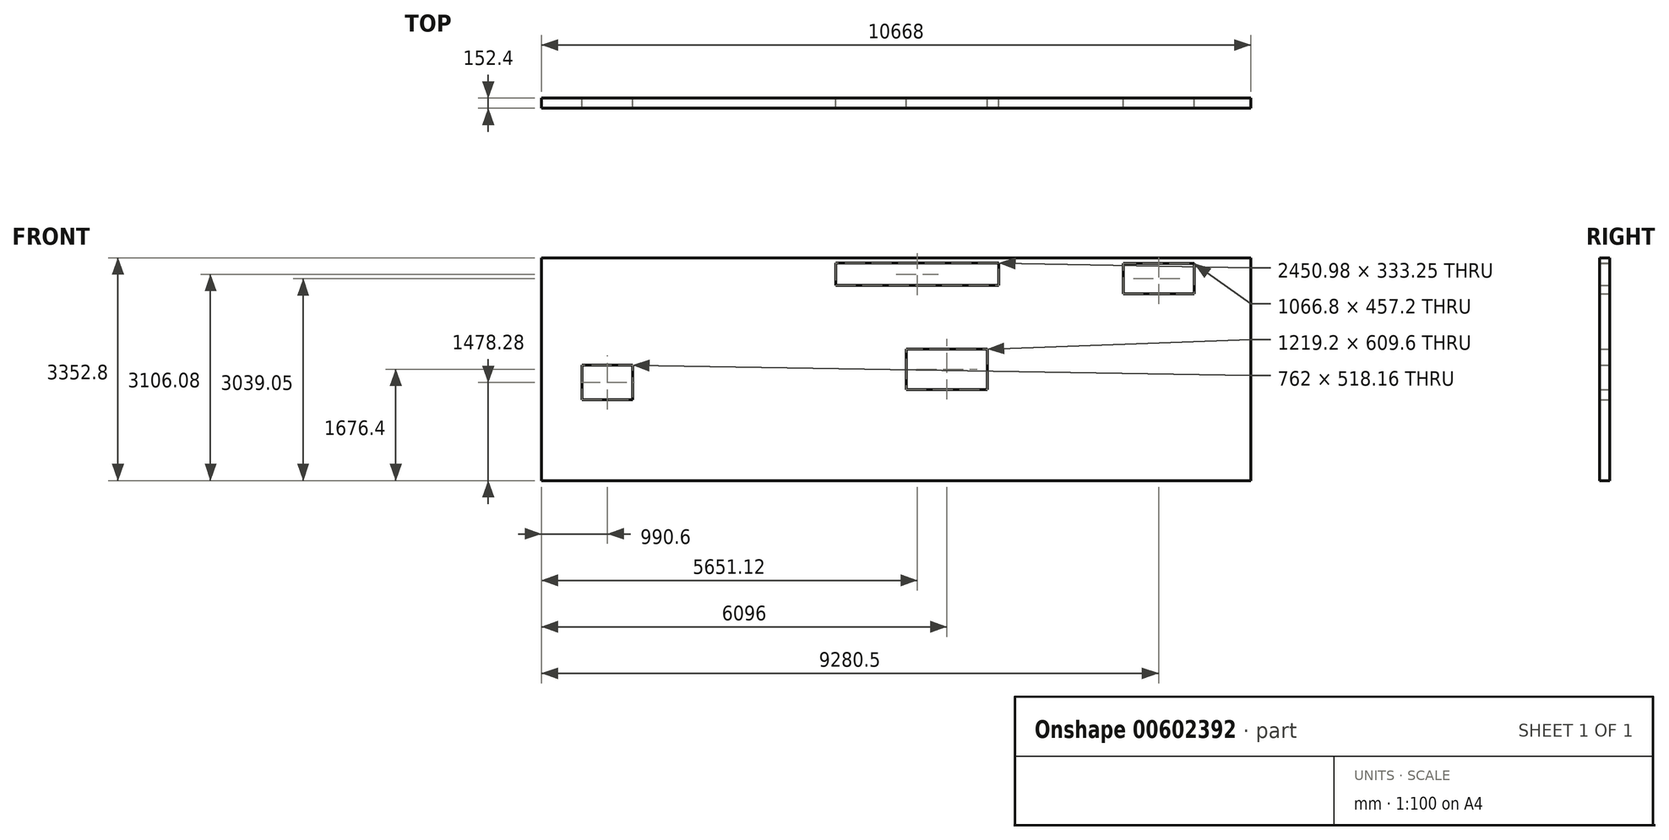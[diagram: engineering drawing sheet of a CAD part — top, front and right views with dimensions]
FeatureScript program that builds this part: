
annotation { "Feature Type Name" : "Feature", "Feature Type Description" : "" }
export const myFeature = defineFeature(function(context is Context, id is Id, definition is map)
    precondition{}
    {
        {
            var Q0;
            Q0=qCreatedBy(makeId("Front.planeOp"),FACE);
            var sketch = newSketch(context, id + "F0", { "sketchPlane" : qUnion([Q0])});
            skLineSegment(sketch, "E0.bottom", {"start": v(-5334, 1676.4) * mm, "end": v(5334, 1676.4) * mm});
            skLineSegment(sketch, "E0.top", {"start": v(-5334, -1676.4) * mm, "end": v(5334, -1676.4) * mm});
            skLineSegment(sketch, "E0.left", {"start": v(-5334, 1676.4) * mm, "end": v(-5334, -1676.4) * mm});
            skLineSegment(sketch, "E0.right", {"start": v(5334, 1676.4) * mm, "end": v(5334, -1676.4) * mm});
            skPoint(sketch, "E0.middle", {"position": v(0, 0) * mm});
            skLineSegment(sketch, "E1.bottom", {"start": v(-4724.4, 60.96) * mm, "end": v(-3962.4, 60.96) * mm});
            skLineSegment(sketch, "E1.top", {"start": v(-4724.4, -457.2) * mm, "end": v(-3962.4, -457.2) * mm});
            skLineSegment(sketch, "E1.left", {"start": v(-4724.4, 60.96) * mm, "end": v(-4724.4, -457.2) * mm});
            skLineSegment(sketch, "E1.right", {"start": v(-3962.4, 60.96) * mm, "end": v(-3962.4, -457.2) * mm});
            skPoint(sketch, "E1.middle", {"position": v(-4343.4, -198.12) * mm});
            skLineSegment(sketch, "E2.bottom", {"start": v(152.4, 304.8) * mm, "end": v(1371.6, 304.8) * mm});
            skLineSegment(sketch, "E2.top", {"start": v(152.4, -304.8) * mm, "end": v(1371.6, -304.8) * mm});
            skLineSegment(sketch, "E2.left", {"start": v(152.4, 304.8) * mm, "end": v(152.4, -304.8) * mm});
            skLineSegment(sketch, "E2.right", {"start": v(1371.6, 304.8) * mm, "end": v(1371.6, -304.8) * mm});
            skPoint(sketch, "E2.middle", {"position": v(762, 0) * mm});
            skLineSegment(sketch, "E3.bottom", {"start": v(3413.1, 1591.25) * mm, "end": v(4479.9, 1591.25) * mm});
            skLineSegment(sketch, "E3.top", {"start": v(3413.1, 1134.05) * mm, "end": v(4479.9, 1134.05) * mm});
            skLineSegment(sketch, "E3.left", {"start": v(3413.1, 1591.25) * mm, "end": v(3413.1, 1134.05) * mm});
            skLineSegment(sketch, "E3.right", {"start": v(4479.9, 1591.25) * mm, "end": v(4479.9, 1134.05) * mm});
            skLineSegment(sketch, "E4.bottom", {"start": v(-908.37, 1596.3) * mm, "end": v(1542.61, 1596.3) * mm});
            skLineSegment(sketch, "E4.top", {"start": v(-908.37, 1263.05) * mm, "end": v(1542.61, 1263.05) * mm});
            skLineSegment(sketch, "E4.left", {"start": v(-908.37, 1596.3) * mm, "end": v(-908.37, 1263.05) * mm});
            skLineSegment(sketch, "E4.right", {"start": v(1542.61, 1596.3) * mm, "end": v(1542.61, 1263.05) * mm});
            skSolve(sketch);
        }
        {
            var Q0;
            Q0=makeQuery(id+"F0.imprint","IMPRINT",FACE,{"disambiguationData":[TD([[makeQuery(id+"F0.imprint","IMPRINT",EDGE,{"derivedFrom":sQuery(id+"F0.wireOp",EDGE,"E0.bottom")}),-1.0]])]});
            extrude(context, id + "F1", {"entities" : qUnion([Q0]), "depth" : 152.4 * mm, "offsetDistance" : 30.48 * mm});
        }
    });
